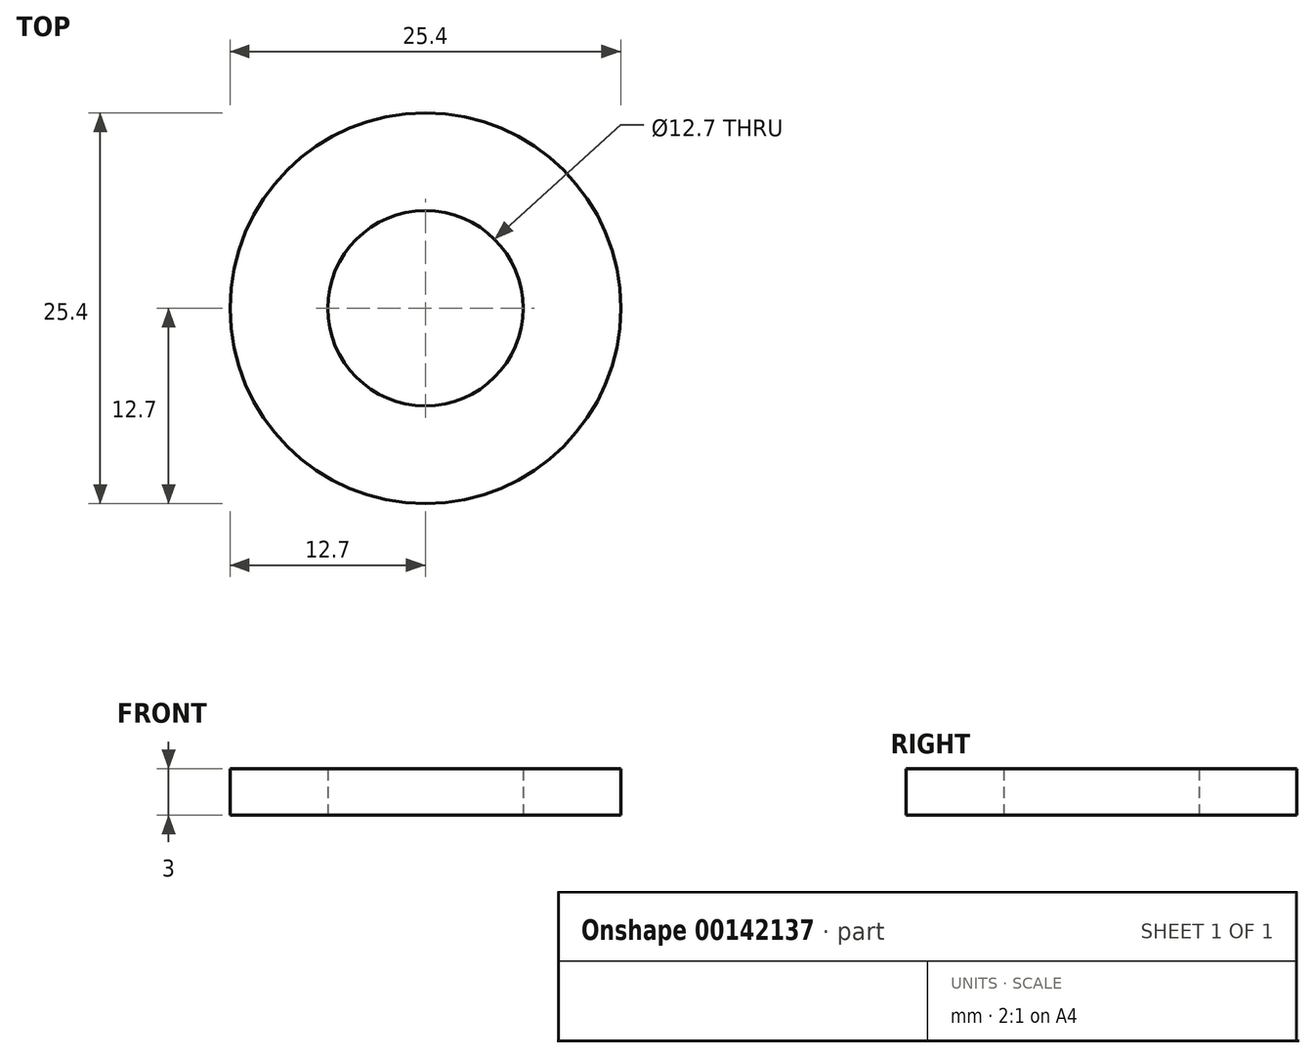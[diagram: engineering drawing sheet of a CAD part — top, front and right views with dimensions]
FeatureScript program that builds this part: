
annotation { "Feature Type Name" : "Feature", "Feature Type Description" : "" }
export const myFeature = defineFeature(function(context is Context, id is Id, definition is map)
    precondition{}
    {
        {
            var Q0;
            Q0=qCreatedBy(makeId("Top.planeOp"),FACE);
            var sketch = newSketch(context, id + "F0", { "sketchPlane" : qUnion([Q0])});
            skCircle(sketch, "E0", {"center": v(0, 0) * mm, "radius": 12.7 * mm});
            skCircle(sketch, "E1", {"center": v(0, 0) * mm, "radius": 6.35 * mm});
            skSolve(sketch);
        }
        {
            var Q0;
            Q0=makeQuery(id+"F0.imprint","IMPRINT",FACE,{"disambiguationData":[TD([[makeQuery(id+"F0.imprint","IMPRINT",EDGE,{"derivedFrom":sQuery(id+"F0.wireOp",EDGE,"E0")}),1.0]])]});
            extrude(context, id + "F1", {"entities" : qUnion([Q0]), "depth" : 3 * mm});
        }
    });
